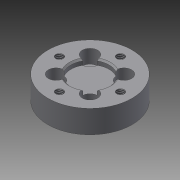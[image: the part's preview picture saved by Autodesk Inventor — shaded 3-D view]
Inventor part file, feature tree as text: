
AUTODESK INVENTOR PART (.ipt)
format: ipt  version: 2013 (Build 170138000, 138)  size: 157,184 bytes
history: native  units: mm
features: extrude x3, sketch x3, hole x3, chamfer x2
ambient origin geometry x8: Origin, YZ Plane, XZ Plane, XY Plane, X Axis, Y Axis, Z Axis, Center Point
bodies: Solid1 (feature_tree)
feature tree (11):
  extrude  "Extrusion1"  Depth=15.0mm TaperAngle=0.0deg
  sketch  "Sketch2"  dims[d3=15.75mm d4=20.0mm]
  extrude  "Extrusion2"  Depth=20.0mm
  hole  "Hole1"  [1 undecoded]
  hole  "Hole2"  [1 undecoded]
  sketch  "Sketch3"  dims[d5=80.0mm d7=360.0deg d9=80.0mm d11=360.0deg d13=25.0mm d14=3.5mm d15=0.0mm d16=5.5mm d17=6.0mm d18=10.0mm d19=9.0mm d20=90.0deg d21=8.0mm d22=20.594885mm d23=4.917mm d24=10.0mm d25=10.0mm d26=5.7mm d27=90.0deg d28=10.0mm d29=20.594885mm d31=15.75mm d32=20.0mm d33=3.0mm d34=8.608mm d35=10.0mm d36=5.7mm d37=90.0deg d38=4.0mm d39=20.594885mm d40=3.0mm d41=0.0mm d42=1.0mm d43=2.0mm d44=45.0deg d45=1.0mm d46=2.0mm d47=45.0deg]
  hole  "Hole3"  [1 undecoded]
  extrude  "Extrusion3"  Depth=15.75mm
  chamfer  "Chamfer1"  Distance=20.0mm
  chamfer  "Chamfer2"  Distance=3.0mm
  sketch  "Sketch1"  dims[d0=55.0mm d1=15.0mm d2=0.0mm]
note: 3 required parameter values undecoded (feature->parameter linkage not recoverable at this tier; creation-order binding heuristic only, values carry confidence <= 0.55)
